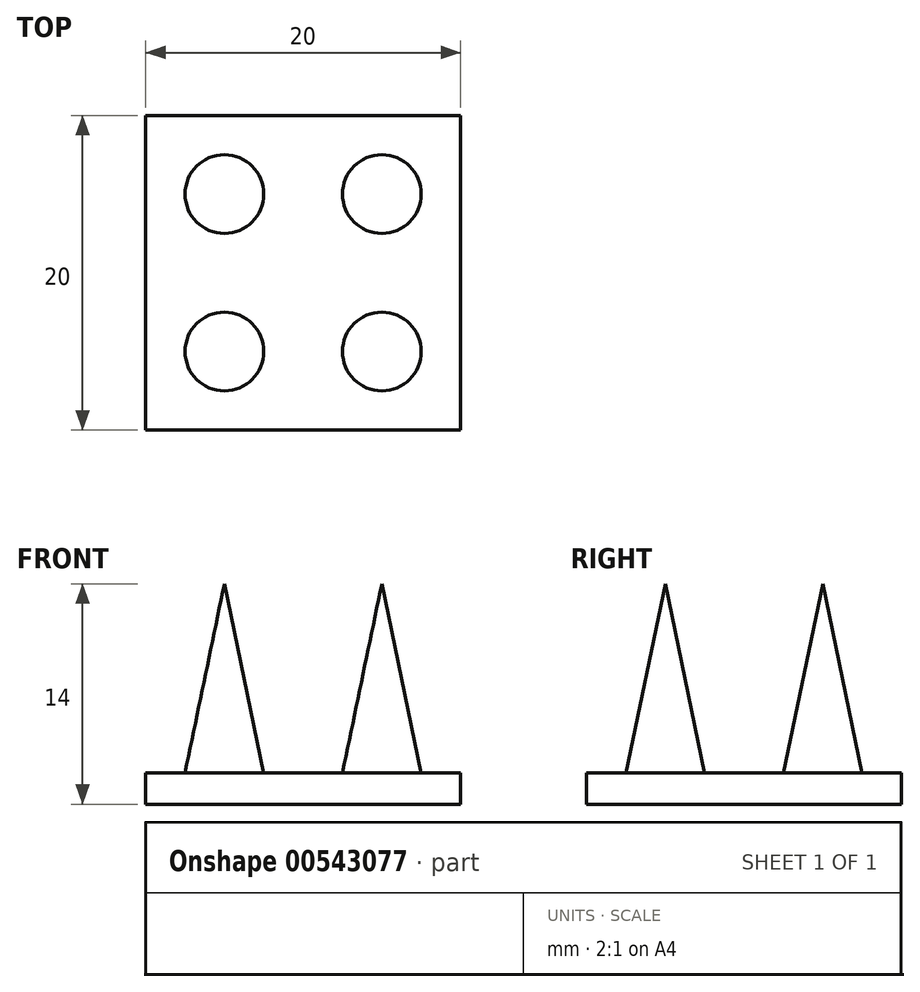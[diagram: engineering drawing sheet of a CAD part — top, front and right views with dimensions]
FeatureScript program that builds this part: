
annotation { "Feature Type Name" : "Feature", "Feature Type Description" : "" }
export const myFeature = defineFeature(function(context is Context, id is Id, definition is map)
    precondition{}
    {
        {
            var Q0;
            Q0=qCreatedBy(makeId("Top.planeOp"),FACE);
            var sketch = newSketch(context, id + "F0", { "sketchPlane" : qUnion([Q0])});
            skLineSegment(sketch, "E0.bottom", {"start": v(0, 0) * mm, "end": v(20, 0) * mm});
            skLineSegment(sketch, "E0.top", {"start": v(0, -20) * mm, "end": v(20, -20) * mm});
            skLineSegment(sketch, "E0.left", {"start": v(0, 0) * mm, "end": v(0, -20) * mm});
            skLineSegment(sketch, "E0.right", {"start": v(20, 0) * mm, "end": v(20, -20) * mm});
            skLineSegment(sketch, "E1", {"start": v(0, -20) * mm, "end": v(10, -10) * mm, "construction": true});
            skLineSegment(sketch, "E2", {"start": v(0, 0) * mm, "end": v(10, -10) * mm, "construction": true});
            skCircle(sketch, "E3", {"center": v(5, -5) * mm, "radius": 2.5 * mm});
            skPoint(sketch, "E4", {"position": v(10, -10) * mm});
            skLineSegment(sketch, "E5", {"start": v(10, -10) * mm, "end": v(20, -20) * mm, "construction": true});
            skLineSegment(sketch, "E6", {"start": v(10, -10) * mm, "end": v(20, 0) * mm, "construction": true});
            skCircle(sketch, "E7", {"center": v(15, -5) * mm, "radius": 2.5 * mm});
            skCircle(sketch, "E8", {"center": v(15, -15) * mm, "radius": 2.5 * mm});
            skCircle(sketch, "E9", {"center": v(5, -15) * mm, "radius": 2.5 * mm});
            skSolve(sketch);
        }
        {
            var Q0;
            Q0 = qSketchRegion(id + "F0", true);
            var Q1;
            Q1=makeQuery(id+"F0.imprint","IMPRINT",FACE,{"disambiguationData":[TD([[makeQuery(id+"F0.imprint","IMPRINT",EDGE,{"derivedFrom":sQuery(id+"F0.wireOp",EDGE,"E3")}),1.0]])]});
            var Q2;
            Q2=makeQuery(id+"F0.imprint","IMPRINT",FACE,{"disambiguationData":[TD([[makeQuery(id+"F0.imprint","IMPRINT",EDGE,{"derivedFrom":sQuery(id+"F0.wireOp",EDGE,"E7")}),1.0]])]});
            var Q3;
            Q3=makeQuery(id+"F0.imprint","IMPRINT",FACE,{"disambiguationData":[TD([[makeQuery(id+"F0.imprint","IMPRINT",EDGE,{"derivedFrom":sQuery(id+"F0.wireOp",EDGE,"E8")}),1.0]])]});
            var Q4;
            Q4=makeQuery(id+"F0.imprint","IMPRINT",FACE,{"disambiguationData":[TD([[makeQuery(id+"F0.imprint","IMPRINT",EDGE,{"derivedFrom":sQuery(id+"F0.wireOp",EDGE,"E9")}),1.0]])]});
            extrude(context, id + "F1", {"entities" : qUnion([Q0, Q1, Q2, Q3, Q4]), "oppositeDirection" : true, "depth" : 2 * mm, "offsetDistance" : 25 * mm});
        }
        {
            var Q0;
            Q0=makeQuery(id+"F0.imprint","IMPRINT",FACE,{"disambiguationData":[TD([[makeQuery(id+"F0.imprint","IMPRINT",EDGE,{"derivedFrom":sQuery(id+"F0.wireOp",EDGE,"E0.bottom")}),-1.0]])]});
            cPlane(context, id + "F2", {"entities" : qUnion([Q0]), "cplaneType" : CPlaneType.OFFSET, "offset" : 12 * mm, "width" : 150 * mm, "height" : 150 * mm});
        }
        {
            var Q0;
            Q0=qCreatedBy(id+"F2.planeOp",FACE);
            var sketch = newSketch(context, id + "F3", { "sketchPlane" : qUnion([Q0])});
            skPoint(sketch, "E10.0", {"position": v(15, -15) * mm});
            skPoint(sketch, "E10.1", {"position": v(15, -5) * mm});
            skPoint(sketch, "E10.2", {"position": v(5, -5) * mm});
            skPoint(sketch, "E10.3", {"position": v(5, -15) * mm});
            skSolve(sketch);
        }
        {
            var Q1;
            Q1=makeQuery(id+"F0.imprint","IMPRINT",FACE,{"disambiguationData":[TD([[makeQuery(id+"F0.imprint","IMPRINT",EDGE,{"derivedFrom":sQuery(id+"F0.wireOp",EDGE,"E8")}),1.0]])]});
            var Q2;
            Q2=sQuery(id+"F3.wireOp",VERTEX,"E10.0");
            loft(context, id + "F4", {"operationType" : NewBodyOperationType.ADD, "sheetProfilesArray" : [{ "sheetProfileEntities" : qUnion([Q1]) }, { "sheetProfileEntities" : qUnion([Q2]) }]});
        }
        {
            var Q1;
            Q1=sQuery(id+"F3.wireOp",VERTEX,"E10.1");
            var Q2;
            Q2=makeQuery(id+"F0.imprint","IMPRINT",FACE,{"disambiguationData":[TD([[makeQuery(id+"F0.imprint","IMPRINT",EDGE,{"derivedFrom":sQuery(id+"F0.wireOp",EDGE,"E7")}),1.0]])]});
            loft(context, id + "F5", {"operationType" : NewBodyOperationType.ADD, "sheetProfilesArray" : [{ "sheetProfileEntities" : qUnion([Q1]) }, { "sheetProfileEntities" : qUnion([Q2]) }]});
        }
        {
            var Q1;
            Q1=makeQuery(id+"F0.imprint","IMPRINT",FACE,{"disambiguationData":[TD([[makeQuery(id+"F0.imprint","IMPRINT",EDGE,{"derivedFrom":sQuery(id+"F0.wireOp",EDGE,"E3")}),1.0]])]});
            var Q2;
            Q2=sQuery(id+"F3.wireOp",VERTEX,"E10.2");
            loft(context, id + "F6", {"operationType" : NewBodyOperationType.ADD, "sheetProfilesArray" : [{ "sheetProfileEntities" : qUnion([Q1]) }, { "sheetProfileEntities" : qUnion([Q2]) }]});
        }
        {
            var Q1;
            Q1=sQuery(id+"F3.wireOp",VERTEX,"E10.3");
            var Q2;
            Q2=makeQuery(id+"F0.imprint","IMPRINT",FACE,{"disambiguationData":[TD([[makeQuery(id+"F0.imprint","IMPRINT",EDGE,{"derivedFrom":sQuery(id+"F0.wireOp",EDGE,"E9")}),1.0]])]});
            loft(context, id + "F7", {"operationType" : NewBodyOperationType.ADD, "sheetProfilesArray" : [{ "sheetProfileEntities" : qUnion([Q1]) }, { "sheetProfileEntities" : qUnion([Q2]) }]});
        }
    });
